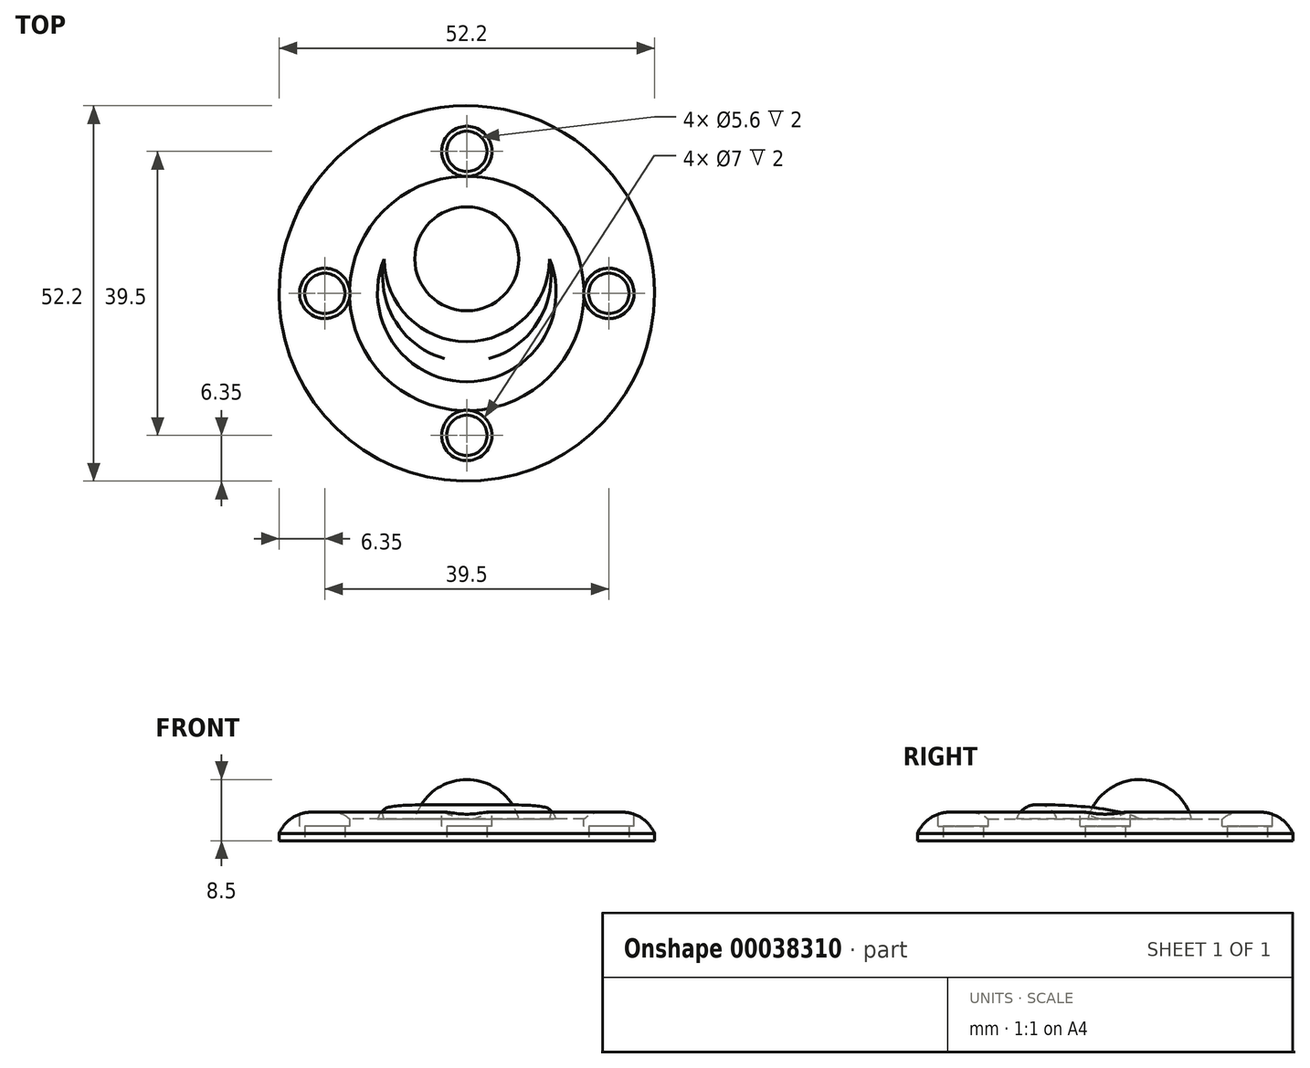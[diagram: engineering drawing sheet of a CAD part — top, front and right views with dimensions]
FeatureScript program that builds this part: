
annotation { "Feature Type Name" : "Feature", "Feature Type Description" : "" }
export const myFeature = defineFeature(function(context is Context, id is Id, definition is map)
    precondition{}
    {
        {
            var Q0;
            Q0=qCreatedBy(makeId("Top.planeOp"),FACE);
            var sketch = newSketch(context, id + "F0", { "sketchPlane" : qUnion([Q0])});
            skCircle(sketch, "E0", {"center": v(0, 0) * mm, "radius": 26.1 * mm});
            skSolve(sketch);
        }
        {
            var Q0;
            Q0 = qSketchRegion(id + "F0", true);
            extrude(context, id + "F1", {"entities" : qUnion([Q0]), "depth" : 3 * mm});
        }
        {
            var Q0;
            Q0=makeQuery(id+"F1.opExtrude","CAP_FACE",FACE,{"disambiguationData":[OSD([sQuery(id+"F0.wireOp",EDGE,"E0")])],"isStart":false});
            var sketch = newSketch(context, id + "F2", { "sketchPlane" : qUnion([Q0])});
            skCircle(sketch, "E1", {"center": v(0, 0) * mm, "radius": 16.3 * mm});
            skSolve(sketch);
        }
        {
            var Q0;
            Q0=makeQuery(id+"F2.imprint","IMPRINT",FACE,{"disambiguationData":[TD([[makeQuery(id+"F2.imprint","IMPRINT",EDGE,{"derivedFrom":sQuery(id+"F2.wireOp",EDGE,"E1")}),1.0]])]});
            extrude(context, id + "F3", {"entities" : qUnion([Q0]), "operationType" : NewBodyOperationType.REMOVE, "oppositeDirection" : true, "depth" : 1 * mm});
        }
        {
            var Q0;
            Q0=makeQuery(id+"F1.opExtrude","CAP_FACE",FACE,{"disambiguationData":[OSD([sQuery(id+"F0.wireOp",EDGE,"E0")])],"isStart":false});
            fillet(context, id + "F4", {"entities" : qUnion([Q0]), "radius" : 5 * mm, "tangentPropagation" : true, "allowEdgeOverflow" : false});
        }
        {
            var Q0;
            Q0=qCreatedBy(makeId("Top.planeOp"),FACE);
            var sketch = newSketch(context, id + "F5", { "sketchPlane" : qUnion([Q0])});
            skLineSegment(sketch, "E2", {"start": v(0, 0) * mm, "end": v(0, 19.75) * mm, "construction": true});
            skCircle(sketch, "E3", {"center": v(0, 19.75) * mm, "radius": 2.8 * mm});
            skCircle(sketch, "E4.1.0", {"center": v(-19.75, 0) * mm, "radius": 2.8 * mm});
            skCircle(sketch, "E4.2.0", {"center": v(0, -19.75) * mm, "radius": 2.8 * mm});
            skCircle(sketch, "E4.3.0", {"center": v(19.75, 0) * mm, "radius": 2.8 * mm});
            skPoint(sketch, "E4.center", {"position": v(0, 0) * mm});
            skSolve(sketch);
        }
        {
            var Q0;
            Q0 = qSketchRegion(id + "F5", true);
            extrude(context, id + "F6", {"entities" : qUnion([Q0]), "operationType" : NewBodyOperationType.REMOVE, "endBound" : BoundingType.THROUGH_ALL, "depth" : 25 * mm});
        }
        {
            var Q0;
            Q0=makeQuery(id+"F3.boolean.opBoolean","COPY",FACE,{"derivedFrom":makeQuery(id+"F3.opExtrude","CAP_FACE",FACE,{"disambiguationData":[OSD([sQuery(id+"F2.wireOp",EDGE,"E1")])],"isStart":false})});
            var sketch = newSketch(context, id + "F7", { "sketchPlane" : qUnion([Q0])});
            skCircle(sketch, "E5", {"center": v(0, 4.8) * mm, "radius": 7.5 * mm, "construction": true});
            skLineSegment(sketch, "E6", {"start": v(0, 16.3) * mm, "end": v(0, 12.3) * mm, "construction": true});
            skLineSegment(sketch, "E7", {"start": v(0, -16.3) * mm, "end": v(0, -12.3) * mm, "construction": true});
            skPoint(sketch, "E7.startSnap0", {"position": v(0, -13.3) * mm});
            skLineSegment(sketch, "E8", {"start": v(0, -6.7) * mm, "end": v(0, -2.7) * mm, "construction": true});
            skArc(sketch, "E9", {"start": v(-11.5, 4.8) * mm, "mid": v(0, -6.7) * mm, "end": v(11.5, 4.8) * mm});
            skArc(sketch, "E10", {"start": v(-11.5, 4.8) * mm, "mid": v(0, -12.3) * mm, "end": v(11.5, 4.8) * mm});
            skLineSegment(sketch, "E11", {"start": v(-11.5, 4.8) * mm, "end": v(-7.5, 4.8) * mm, "construction": true});
            skLineSegment(sketch, "E12", {"start": v(11.5, 4.8) * mm, "end": v(7.5, 4.8) * mm, "construction": true});
            skLineSegment(sketch, "E13", {"start": v(0, 12.3) * mm, "end": v(0, -2.7) * mm});
            skArc(sketch, "E14", {"start": v(0, -2.7) * mm, "mid": v(7.5, 4.8) * mm, "end": v(0, 12.3) * mm});
            skSolve(sketch);
        }
        {
            var Q0;
            Q0=makeQuery(id+"F7.imprint","IMPRINT",FACE,{"disambiguationData":[TD([[makeQuery(id+"F7.imprint","IMPRINT",EDGE,{"derivedFrom":sQuery(id+"F7.wireOp",EDGE,"E9")}),-1.0]])]});
            extrude(context, id + "F8", {"entities" : qUnion([Q0]), "operationType" : NewBodyOperationType.ADD, "depth" : 2 * mm});
        }
        {
            var Q0;
            Q0=makeQuery(id+"F8.opExtrude","CAP_FACE",FACE,{"disambiguationData":[OSD([sQuery(id+"F7.wireOp",EDGE,"E9"),sQuery(id+"F7.wireOp",EDGE,"E10")])],"isStart":false});
            fillet(context, id + "F9", {"entities" : qUnion([Q0]), "radius" : 2.85 * mm, "tangentPropagation" : true, "allowEdgeOverflow" : false});
        }
        {
            var Q0;
            Q0=qCreatedBy(makeId("Top.planeOp"),FACE);
            cPlane(context, id + "F10", {"entities" : qUnion([Q0]), "cplaneType" : CPlaneType.OFFSET, "offset" : 3 * mm, "width" : 150 * mm, "height" : 150 * mm});
        }
        {
            var Q0;
            Q0=qCreatedBy(id+"F10.planeOp",FACE);
            var sketch = newSketch(context, id + "F11", { "sketchPlane" : qUnion([Q0])});
            skCircle(sketch, "E15.0", {"center": v(0, 19.75) * mm, "radius": 2.8 * mm, "construction": true});
            skCircle(sketch, "E16.0", {"center": v(-19.75, 0) * mm, "radius": 2.8 * mm, "construction": true});
            skCircle(sketch, "E17.0", {"center": v(0, -19.75) * mm, "radius": 2.8 * mm, "construction": true});
            skCircle(sketch, "E18.0", {"center": v(19.75, 0) * mm, "radius": 2.8 * mm, "construction": true});
            skCircle(sketch, "E19", {"center": v(0, 19.75) * mm, "radius": 3.5 * mm});
            skCircle(sketch, "E20", {"center": v(19.75, 0) * mm, "radius": 3.5 * mm});
            skCircle(sketch, "E21", {"center": v(0, -19.75) * mm, "radius": 3.5 * mm});
            skCircle(sketch, "E22", {"center": v(-19.75, 0) * mm, "radius": 3.5 * mm});
            skSolve(sketch);
        }
        {
            var Q0;
            Q0 = qSketchRegion(id + "F11", true);
            extrude(context, id + "F12", {"entities" : qUnion([Q0]), "operationType" : NewBodyOperationType.REMOVE, "oppositeDirection" : true, "depth" : 2 * mm});
        }
        {
            var Q0;
            Q0=qCreatedBy(makeId("Top.planeOp"),FACE);
            var sketch = newSketch(context, id + "F13", { "sketchPlane" : qUnion([Q0])});
            skArc(sketch, "E23.0.0", {"start": v(0, -2.7) * mm, "mid": v(7.5, 4.8) * mm, "end": v(0, 12.3) * mm});
            skLineSegment(sketch, "E23.0.1", {"start": v(0, 12.3) * mm, "end": v(0, -2.7) * mm});
            skSolve(sketch);
        }
        {
            var Q0;
            Q0=makeQuery(id+"F13.imprint","IMPRINT",FACE,{"disambiguationData":[TD([[makeQuery(id+"F13.imprint","IMPRINT",EDGE,{"derivedFrom":sQuery(id+"F13.wireOp",EDGE,"E23.0.0")}),1.0]])]});
            var Q1;
            Q1=sQuery(id+"F13.wireOp",EDGE,"E23.0.1");
            revolve(context, id + "F14", {"operationType" : NewBodyOperationType.ADD, "entities" : qUnion([Q0]), "axis" : qUnion([Q1]), "revolveType" : RevolveType.ONE_DIRECTION, "angle" : 180 * degree});
        }
        {
            var Q0;
            Q0=makeQuery(id+"F1.opExtrude","SWEPT_BODY",BODY,{"disambiguationData":[OSD([sQuery(id+"F0.wireOp",EDGE,"E0")])]});
            transform(context, id + "F15", {"entities" : qUnion([Q0]), "transformType" : TransformType.TRANSLATION_3D, "dx" : 0 * mm, "dy" : 0 * mm, "dz" : 1 * mm, "makeCopy" : false});
        }
        {
            var Q0;
            Q0=makeQuery(id+"F1.opExtrude","CAP_FACE",FACE,{"disambiguationData":[OSD([sQuery(id+"F0.wireOp",EDGE,"E0")])],"isStart":true});
            var sketch = newSketch(context, id + "F16", { "sketchPlane" : qUnion([Q0])});
            skCircle(sketch, "E24.0", {"center": v(0, 0) * mm, "radius": 26.1 * mm});
            skCircle(sketch, "E25.0", {"center": v(0, 19.75) * mm, "radius": 2.8 * mm});
            skCircle(sketch, "E26.0", {"center": v(-19.75, 0) * mm, "radius": 2.8 * mm});
            skCircle(sketch, "E27.0", {"center": v(0, -19.75) * mm, "radius": 2.8 * mm});
            skCircle(sketch, "E28.0", {"center": v(19.75, 0) * mm, "radius": 2.8 * mm});
            skSolve(sketch);
        }
        {
            var Q0;
            Q0 = qSketchRegion(id + "F16", true);
            extrude(context, id + "F17", {"entities" : qUnion([Q0]), "operationType" : NewBodyOperationType.ADD, "depth" : 1 * mm});
        }
    });
